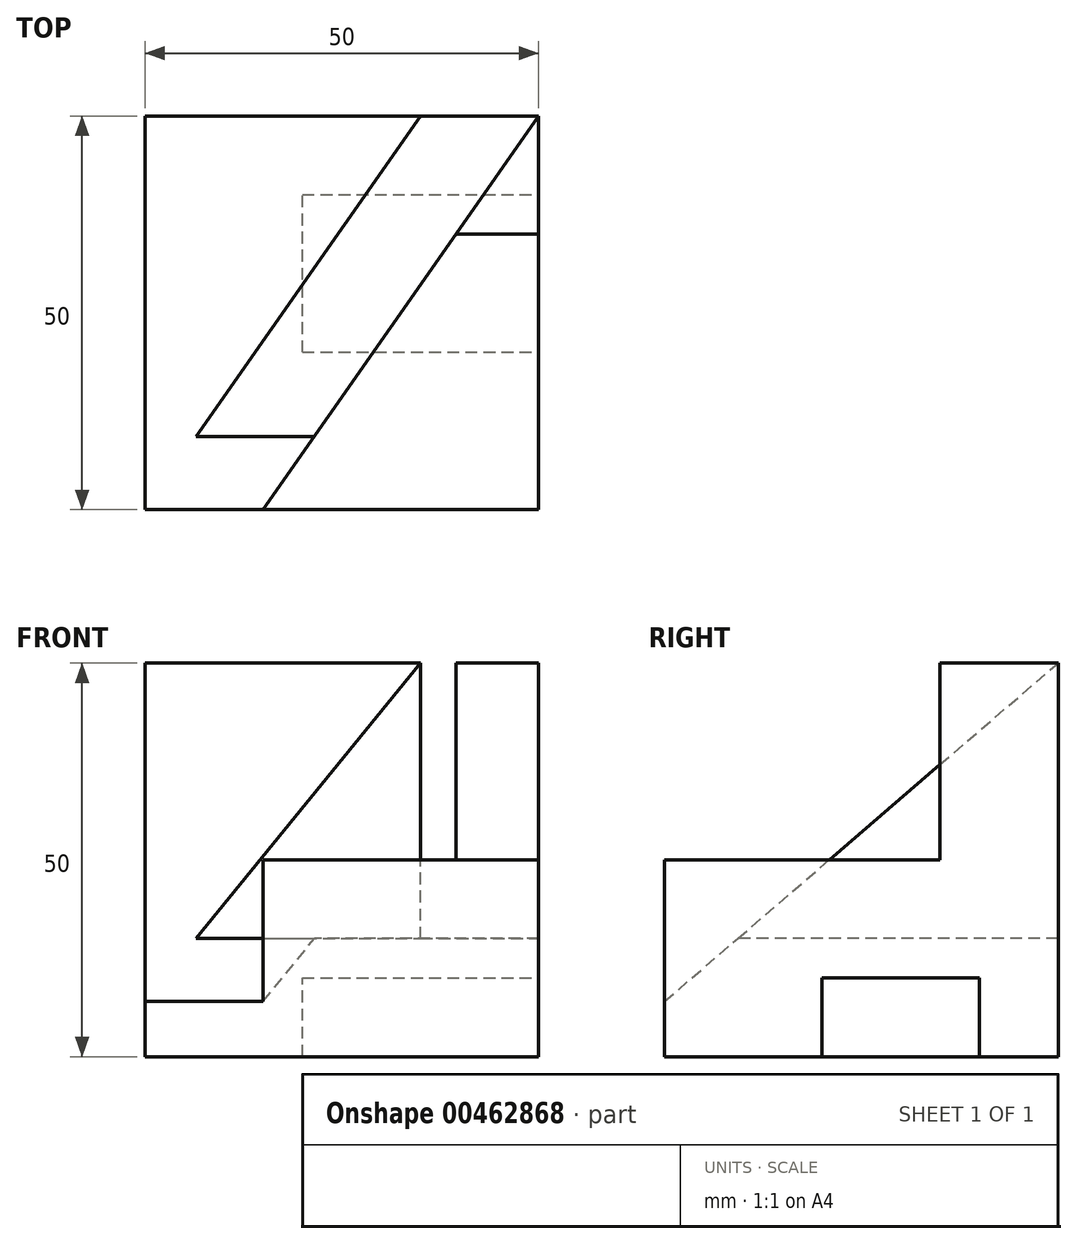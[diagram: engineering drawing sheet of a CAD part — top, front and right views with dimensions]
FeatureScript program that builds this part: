
annotation { "Feature Type Name" : "Feature", "Feature Type Description" : "" }
export const myFeature = defineFeature(function(context is Context, id is Id, definition is map)
    precondition{}
    {
        {
            var Q0;
            Q0=qCreatedBy(makeId("Top.planeOp"),FACE);
            var sketch = newSketch(context, id + "F0", { "sketchPlane" : qUnion([Q0])});
            skLineSegment(sketch, "E0.bottom", {"start": v(0, 0) * mm, "end": v(50, 0) * mm});
            skLineSegment(sketch, "E0.top", {"start": v(0, 50) * mm, "end": v(50, 50) * mm});
            skLineSegment(sketch, "E0.left", {"start": v(0, 0) * mm, "end": v(0, 50) * mm});
            skLineSegment(sketch, "E0.right", {"start": v(50, 0) * mm, "end": v(50, 50) * mm});
            skSolve(sketch);
        }
        {
            var Q0;
            Q0 = qSketchRegion(id + "F0", true);
            extrude(context, id + "F1", {"entities" : qUnion([Q0]), "depth" : 50 * mm});
        }
        {
            var Q0;
            Q0=makeQuery(id+"F1.opExtrude","CAP_FACE",FACE,{"disambiguationData":[OSD([sQuery(id+"F0.wireOp",EDGE,"E0.bottom"),sQuery(id+"F0.wireOp",EDGE,"E0.top"),sQuery(id+"F0.wireOp",EDGE,"E0.left"),sQuery(id+"F0.wireOp",EDGE,"E0.right")])],"isStart":true});
            cPlane(context, id + "F2", {"entities" : qUnion([Q0]), "cplaneType" : CPlaneType.OFFSET, "offset" : 15 * mm, "oppositeDirection" : true, "width" : 150 * mm, "height" : 150 * mm});
        }
        {
            var Q0;
            Q0=makeQuery(id+"F1.opExtrude","CAP_FACE",FACE,{"disambiguationData":[OSD([sQuery(id+"F0.wireOp",EDGE,"E0.bottom"),sQuery(id+"F0.wireOp",EDGE,"E0.top"),sQuery(id+"F0.wireOp",EDGE,"E0.left"),sQuery(id+"F0.wireOp",EDGE,"E0.right")])],"isStart":false});
            var sketch = newSketch(context, id + "F3", { "sketchPlane" : qUnion([Q0])});
            skLineSegment(sketch, "E1", {"start": v(0, 0) * mm, "end": v(35, 50) * mm});
            skLineSegment(sketch, "E2", {"start": v(35, 50) * mm, "end": v(50, 50) * mm});
            skLineSegment(sketch, "E3", {"start": v(50, 50) * mm, "end": v(15, 0) * mm});
            skLineSegment(sketch, "E4", {"start": v(15, 0) * mm, "end": v(0, 0) * mm});
            skSolve(sketch);
        }
        {
            var Q0;
            Q0 = qSketchRegion(id + "F3", true);
            var Q1;
            Q1=qCreatedBy(id+"F2.planeOp",FACE);
            extrude(context, id + "F4", {"entities" : qUnion([Q0]), "operationType" : NewBodyOperationType.REMOVE, "endBound" : BoundingType.UP_TO_SURFACE, "oppositeDirection" : true, "endBoundEntityFace" : qUnion([Q1]), "depth" : 25 * mm});
        }
        {
            var Q0;
            Q0=makeQuery(id+"F1.opExtrude","SWEPT_FACE",FACE,{"disambiguationData":[OSD([sQuery(id+"F0.wireOp",EDGE,"E0.right")])]});
            var sketch = newSketch(context, id + "F5", { "sketchPlane" : qUnion([Q0])});
            skPoint(sketch, "E5.oppositeSnap0", {"position": v(0, 25) * mm});
            skLineSegment(sketch, "E5.bottom", {"start": v(0, 50) * mm, "end": v(35, 50) * mm});
            skLineSegment(sketch, "E5.top", {"start": v(0, 25) * mm, "end": v(35, 25) * mm});
            skLineSegment(sketch, "E5.left", {"start": v(0, 50) * mm, "end": v(0, 25) * mm});
            skLineSegment(sketch, "E5.right", {"start": v(35, 50) * mm, "end": v(35, 25) * mm});
            skSolve(sketch);
        }
        {
            var Q0;
            Q0 = qSketchRegion(id + "F5", true);
            var Q1;
            Q1=makeQuery(id+"F4.boolean.opBoolean","COPY",FACE,{"derivedFrom":makeQuery(id+"F4.opExtrude","SWEPT_FACE",FACE,{"disambiguationData":[OSD([sQuery(id+"F3.wireOp",EDGE,"E3")])]})});
            var Q2;
            Q2=makeQuery(id+"F4.boolean.opBoolean","COPY",FACE,{"derivedFrom":makeQuery(id+"F4.opExtrude","SWEPT_FACE",FACE,{"disambiguationData":[OSD([sQuery(id+"F3.wireOp",EDGE,"E3")])]})});
            var Q3;
            Q3=makeQuery(id+"F1.opExtrude","SWEPT_BODY",BODY,{"disambiguationData":[OSD([sQuery(id+"F0.wireOp",EDGE,"E0.bottom"),sQuery(id+"F0.wireOp",EDGE,"E0.top"),sQuery(id+"F0.wireOp",EDGE,"E0.left"),sQuery(id+"F0.wireOp",EDGE,"E0.right")])]});
            extrude(context, id + "F6", {"entities" : qUnion([Q0, Q1]), "operationType" : NewBodyOperationType.REMOVE, "endBound" : BoundingType.UP_TO_NEXT, "oppositeDirection" : true, "endBoundEntityFace" : qUnion([Q2]), "endBoundEntityBody" : qUnion([Q3]), "depth" : 25 * mm});
        }
        {
            var Q0;
            Q0=makeQuery(id+"F1.opExtrude","SWEPT_FACE",FACE,{"disambiguationData":[OSD([sQuery(id+"F0.wireOp",EDGE,"E0.left")])]});
            var sketch = newSketch(context, id + "F7", { "sketchPlane" : qUnion([Q0])});
            skLineSegment(sketch, "E6", {"start": v(-50, 50) * mm, "end": v(0, 7) * mm});
            skLineSegment(sketch, "E7", {"start": v(0, 7) * mm, "end": v(0, 0) * mm});
            skLineSegment(sketch, "E8", {"start": v(0, 0) * mm, "end": v(-50, 0) * mm});
            skLineSegment(sketch, "E9", {"start": v(-50, 0) * mm, "end": v(-50, 50) * mm});
            skSolve(sketch);
        }
        {
            var Q0;
            {var subQ0=sQuery(id+"F7.wireOp",EDGE,"E6");Q0=makeQuery(id+"F7.imprint","IMPRINT",FACE,{"disambiguationData":[TD([[makeQuery(id+"F7.imprint","IMPRINT",EDGE,{"derivedFrom":subQ0}),1.0]])]});}
            var Q1;
            Q1=makeQuery(id+"F4.boolean.opBoolean","COPY",FACE,{"derivedFrom":makeQuery(id+"F4.opExtrude","SWEPT_FACE",FACE,{"disambiguationData":[OSD([sQuery(id+"F3.wireOp",EDGE,"E3")])]})});
            extrude(context, id + "F8", {"entities" : qUnion([Q0]), "operationType" : NewBodyOperationType.REMOVE, "endBound" : BoundingType.UP_TO_SURFACE, "oppositeDirection" : true, "endBoundEntityFace" : qUnion([Q1]), "depth" : 25 * mm});
        }
        {
            var Q0;
            Q0=makeQuery(id+"F1.opExtrude","SWEPT_FACE",FACE,{"disambiguationData":[OSD([sQuery(id+"F0.wireOp",EDGE,"E0.right")])]});
            var sketch = newSketch(context, id + "F9", { "sketchPlane" : qUnion([Q0])});
            skLineSegment(sketch, "E10.bottom", {"start": v(20, 0) * mm, "end": v(40, 0) * mm});
            skLineSegment(sketch, "E10.top", {"start": v(20, 10) * mm, "end": v(40, 10) * mm});
            skLineSegment(sketch, "E10.left", {"start": v(20, 0) * mm, "end": v(20, 10) * mm});
            skLineSegment(sketch, "E10.right", {"start": v(40, 0) * mm, "end": v(40, 10) * mm});
            skSolve(sketch);
        }
        {
            var Q0;
            Q0=makeQuery(id+"F1.opExtrude","SWEPT_FACE",FACE,{"disambiguationData":[OSD([sQuery(id+"F0.wireOp",EDGE,"E0.left")])]});
            cPlane(context, id + "F10", {"entities" : qUnion([Q0]), "cplaneType" : CPlaneType.OFFSET, "offset" : 20 * mm, "oppositeDirection" : true, "width" : 150 * mm, "height" : 150 * mm});
        }
        {
            var Q0;
            Q0=makeQuery(id+"F9.imprint","IMPRINT",FACE,{"disambiguationData":[TD([[makeQuery(id+"F9.imprint","IMPRINT",EDGE,{"derivedFrom":sQuery(id+"F9.wireOp",EDGE,"E10.bottom")}),1.0]])]});
            var Q1;
            Q1=qCreatedBy(id+"F10.planeOp",FACE);
            extrude(context, id + "F11", {"entities" : qUnion([Q0]), "operationType" : NewBodyOperationType.REMOVE, "endBound" : BoundingType.UP_TO_SURFACE, "oppositeDirection" : true, "endBoundEntityFace" : qUnion([Q1]), "depth" : 25 * mm});
        }
    });
